# Revit family: Roman_Tub_Filler-American_Standard-Town_Square-T45590X
name_source: partatom
category: Plumbing Fixtures
revit_build: Autodesk Revit 2014 (Build: 20130308_1515(x64)
units: mm (PartAtom-declared; Revit-internal decimal feet)

## types (2) — shared parameters
ADA Compliant = Yes
Assembly Code = D2020300
CW Connection = Yes
CWFU = 3
Cold Water Connection Diameter = 1/2"
Cold Water Connection Radius = 1/4"
Default Elevation = 0"
Finish = Metal-American Standard-002-Polished Chrome
Flow Rate = 1.2 gpm/ 4.5 L/min.
HW Connection = Yes
HWFU = 3
Hand Shower = 12"
Height = 4 3/8"
Hot Water Connection Diameter = 1"
Hot Water Connection Radius = 1/4"
Installation Type = Deck Mounted
Length = 12"
Manufacturer = American Standard
Material = Brass-American Standard-002-Polished Chrome
Price = Prices may vary. Please consult Manufacturer Representative for most up-to-date price list.
Product Documentation Link = https://www.americanstandard-us.com
Product Page URL = https://www.americanstandard-us.com
Specification = Two handle deck-mount tub filler shall feature cast brass construction. Shall also feature 1/4 turn washerless ceramic disc valve cartridges.
URL = https://www.americanstandard-us.com
Vent Connection = No
WFU = 4
Warranty Information = Limited Lifetime Function and Finish Warranty
Waste Connection = No
Width = 2 3/16"

## per-type parameters (varying)
| type | Description | R900 Universal Roman Tub Filler Rough Body – Less Personal Shower | R910 Universal Roman Tub Filler Rough Body – WITH Personal Shower | Shower | Shower Connection Description | Shower Connection Size |
| T455900 | T455900 Roman Tub Filler Trim Less Personal Shower, R900 Universal Roman Tub Filler Rough Body – Less Personal Shower | Yes | No | No |  | 0" |
| T455901 | T455901 Roman Tub Filler Trim WITH Personal Shower, R910 Universal Roman Tub Filler Rough Body – WITH Personal Shower | No | Yes | Yes | 1/2'' Global Inlet Connection | 1/2" |

note: column(s) folded — value = type name in every type: Model

## geometry (parser evidence)
native form markers: Sweep x3
no freeform markers — native parametric forms only
